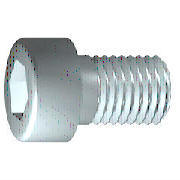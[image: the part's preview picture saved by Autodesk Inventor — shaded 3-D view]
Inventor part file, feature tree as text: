
AUTODESK INVENTOR PART (.ipt)
format: ipt  version: 2020 (Build 240168000, 168)  size: 192,512 bytes
history: native  units: mm (DEFAULTED — no unit token found)
features: sketch x2, other x1, extrude x1, plane x1, fillet x1
ambient origin geometry x7: Origin, YZ Plane, XY Plane, X Axis, Y Axis, Z Axis, Center Point
bodies: Solid1 (feature_tree)
feature tree (6):
  other  "Bryła"
  extrude  "Szczelina"  Depth=10.75mm
  plane  "Work Plane1"
  fillet  "Fillet2"  Radius=0.306825mm
  sketch  "Szkic1"
  sketch  "Szkic2"
